# Revit family: NLRS_57_AIR_UN_exhaust rain hood vrk-vrkg LT_velu
name_source: partatom
category: Air Terminals
units: mm (PartAtom-declared; Revit-internal decimal feet)

## family parameters
Always vertical = No
Cut with Voids When Loaded = No
Part Type = Normal
Room Calculation Point = No
Round Connector Dimension = Use Diameter
Shared = No
Work Plane-Based = No

## types (2) — shared parameters
Assembly Code = 57.00
Description = Velu uitblaas regenkap met of zonder gaas, type VRKG en VRK
FireRating = 00
IfcDescription = Velu uitblaas regenkap met of zonder gaas, type VRKG en VRK
IfcExportAs = IfcAirterminal
IfcExportType = Diffuser
IsExternal = Yes
LoadBearing = No
LookupTable = VRKG
Manufacturer = Velu Ventilatietechniek BV
Model = VRK/VRKG
NLRS_C_content_datum_uitgifte = 23-02-2022
NLRS_C_content_provider = Velu Ventliatietechniek BV
NLRS_C_content_versie = 3.19.01
NLRS_C_description = Velu uitblaas regenkap met of zonder gaas, type VRKG en VRK
NLRS_C_niveau ontwikkeling = LOD400
URL = https://velu.nl

## per-type parameters (varying)
| type | SACS_Base_Index | VELU_Gaas | VELU_Geen_Gaas |
| Regenkap | 0 | No | Yes |
| Regenkap met gaas | 1 | Yes | No |

## geometry (parser evidence)
native form markers: Sweep x5
no freeform markers — native parametric forms only
